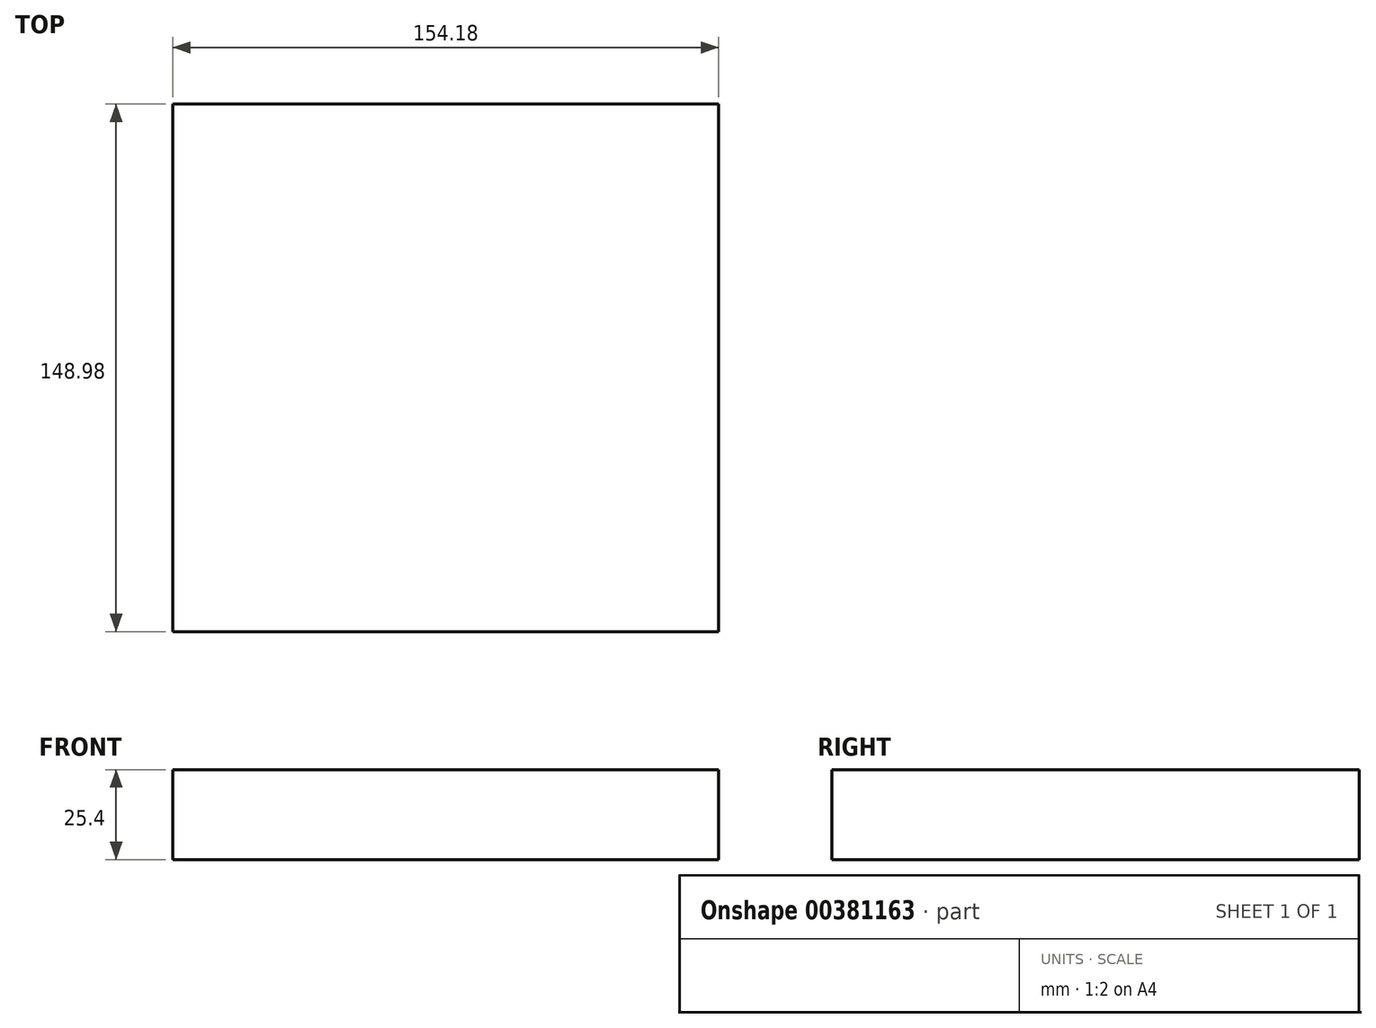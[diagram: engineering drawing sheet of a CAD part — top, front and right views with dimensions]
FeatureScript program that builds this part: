
annotation { "Feature Type Name" : "Feature", "Feature Type Description" : "" }
export const myFeature = defineFeature(function(context is Context, id is Id, definition is map)
    precondition{}
    {
        {
            var Q0;
            Q0=qCreatedBy(makeId("Top.planeOp"),FACE);
            var sketch = newSketch(context, id + "F0", { "sketchPlane" : qUnion([Q0])});
            skLineSegment(sketch, "E0.bottom", {"start": v(77.09, 74.49) * mm, "end": v(-77.09, 74.49) * mm});
            skLineSegment(sketch, "E0.top", {"start": v(77.09, -74.49) * mm, "end": v(-77.09, -74.49) * mm});
            skLineSegment(sketch, "E0.left", {"start": v(77.09, 74.49) * mm, "end": v(77.09, -74.49) * mm});
            skLineSegment(sketch, "E0.right", {"start": v(-77.09, 74.49) * mm, "end": v(-77.09, -74.49) * mm});
            skPoint(sketch, "E0.middle", {"position": v(0, 0) * mm});
            skSolve(sketch);
        }
        {
            var Q0;
            Q0 = qSketchRegion(id + "F0", true);
            extrude(context, id + "F1", {"entities" : qUnion([Q0]), "depth" : 25.4 * mm});
        }
    });
